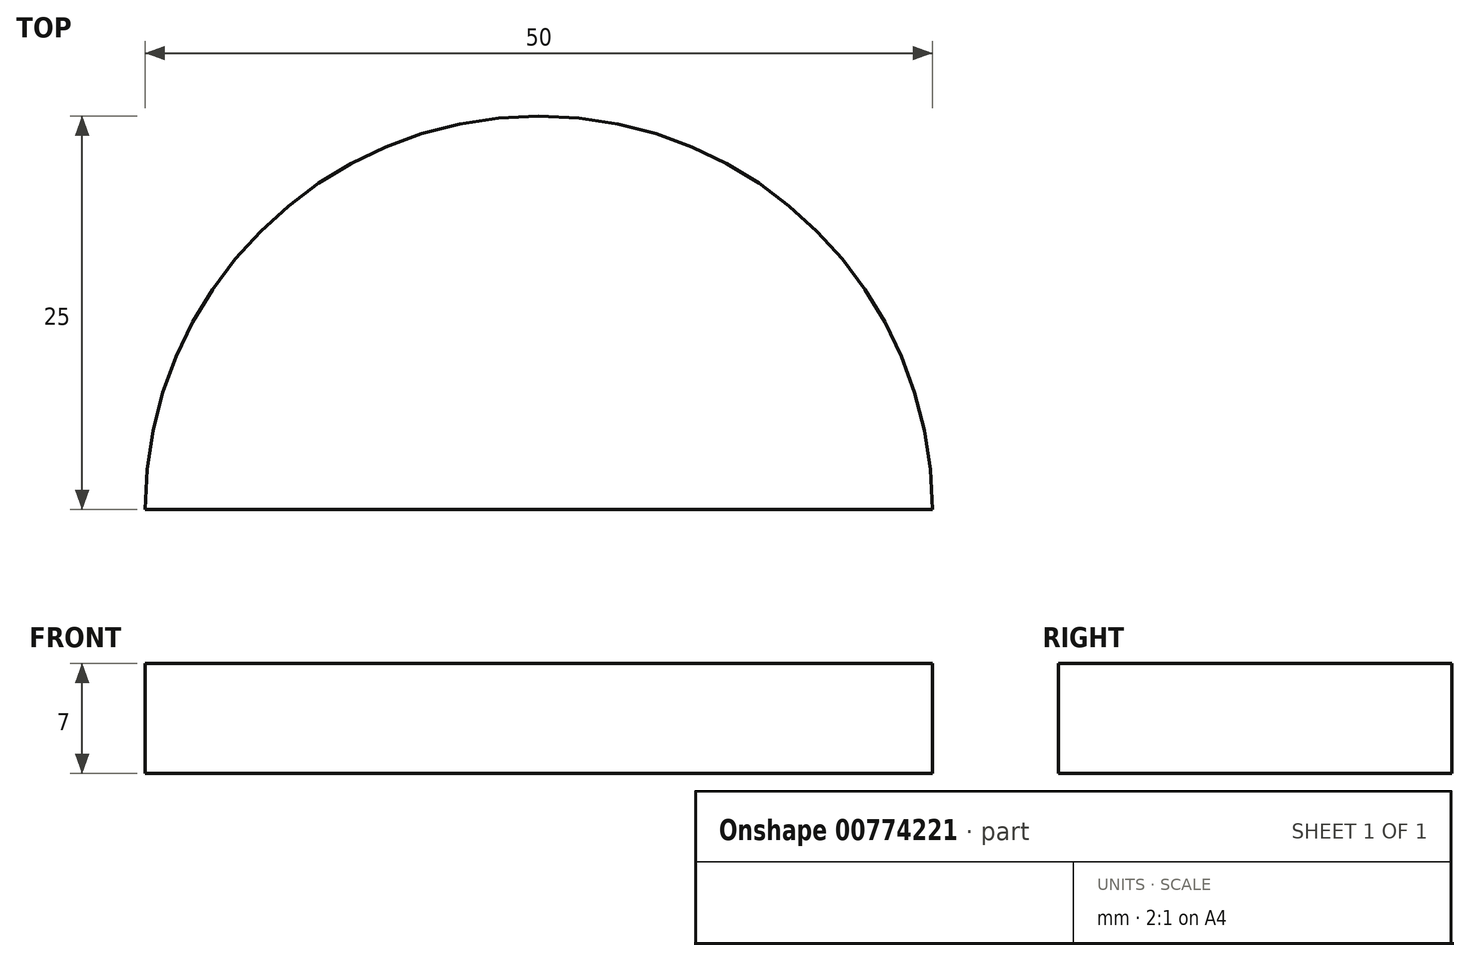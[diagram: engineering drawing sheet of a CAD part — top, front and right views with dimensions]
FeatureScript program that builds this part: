
annotation { "Feature Type Name" : "Feature", "Feature Type Description" : "" }
export const myFeature = defineFeature(function(context is Context, id is Id, definition is map)
    precondition{}
    {
        {
            var Q0;
            Q0=qCreatedBy(makeId("Top.planeOp"),FACE);
            var sketch = newSketch(context, id + "F0", { "sketchPlane" : qUnion([Q0])});
            skCircle(sketch, "E0", {"center": v(0, 0) * mm, "radius": 11 * mm});
            skLineSegment(sketch, "E1.bottom", {"start": v(-25, 47.83) * mm, "end": v(25, 47.83) * mm});
            skLineSegment(sketch, "E1.top", {"start": v(-25, -47.83) * mm, "end": v(25, -47.83) * mm});
            skLineSegment(sketch, "E1.left", {"start": v(-25, 47.83) * mm, "end": v(-25, -47.83) * mm});
            skLineSegment(sketch, "E1.right", {"start": v(25, 47.83) * mm, "end": v(25, -47.83) * mm});
            skArc(sketch, "E2", {"start": v(25, 47.83) * mm, "mid": v(0, 72.83) * mm, "end": v(-25, 47.83) * mm});
            skSolve(sketch);
        }
        {
            var Q0;
            Q0=makeQuery(id+"F0.imprint","IMPRINT",FACE,{"disambiguationData":[TD([[makeQuery(id+"F0.imprint","IMPRINT",EDGE,{"derivedFrom":sQuery(id+"F0.wireOp",EDGE,"E1.bottom")}),1.0]])]});
            extrude(context, id + "F1", {"entities" : qUnion([Q0]), "depth" : 7 * mm, "offsetDistance" : 25 * mm});
        }
    });
